# Revit family: FP_Revit_18_DW60UZ6B_Dishwasher_90000926A
name_source: partatom
category: Specialty Equipment
revit_build: Autodesk Revit 2018 (Build: 20170223_1515(x64)
units: mm (PartAtom-declared; Revit-internal decimal feet)

## family parameters
Always vertical = Yes
Cut with Voids When Loaded = Yes
OmniClass Number = 23.40.40.14.31
OmniClass Title = Cleaning and Disposal Equipment
Part Type = Normal
Room Calculation Point = No
Round Connector Dimension = Use Diameter
Shared = No
Work Plane-Based = No

## types (1)
- FP_Revit_18_DW60UZ6B_Dishwasher_90000926A
    Cavity - Depth = 574 mm  [stored 1.8832 ft]
    Cavity - Width = 600 mm  [stored 1.9685 ft]
    Connector Description - Electrical = 220-240 V, 50 Hz, 10 A
    Connector Description - Sanitary = Drain Hose, No Fitting Required
    Connector Description - Water = 3/4“ BSP (GB20) to suit Flat Washer
    Description = 60cm Dishwasher
    Manufacturer = Fisher & Paykel Appliances
    Material - Body = Fisher & Paykel - Grey
    Material - Door Front = Fisher & Paykel - Glass, Black
    Material - Door Structure = Fisher & Paykel - Black
    Material - Trim = Fisher & Paykel - Black
    Model = DW60UZ6B
    Product - Depth = 572 mm
    Product - Width = 598 mm  [stored 1.96194 ft]
    URL = www.fisherpaykel.com
    Visibility - Clearance Required = Yes

note: [stored X ft] marks values corroborated as IEEE doubles in the binary element streams (Revit-internal decimal feet)

## geometry (parser evidence)
native form markers: Sweep x5
no freeform markers — native parametric forms only
